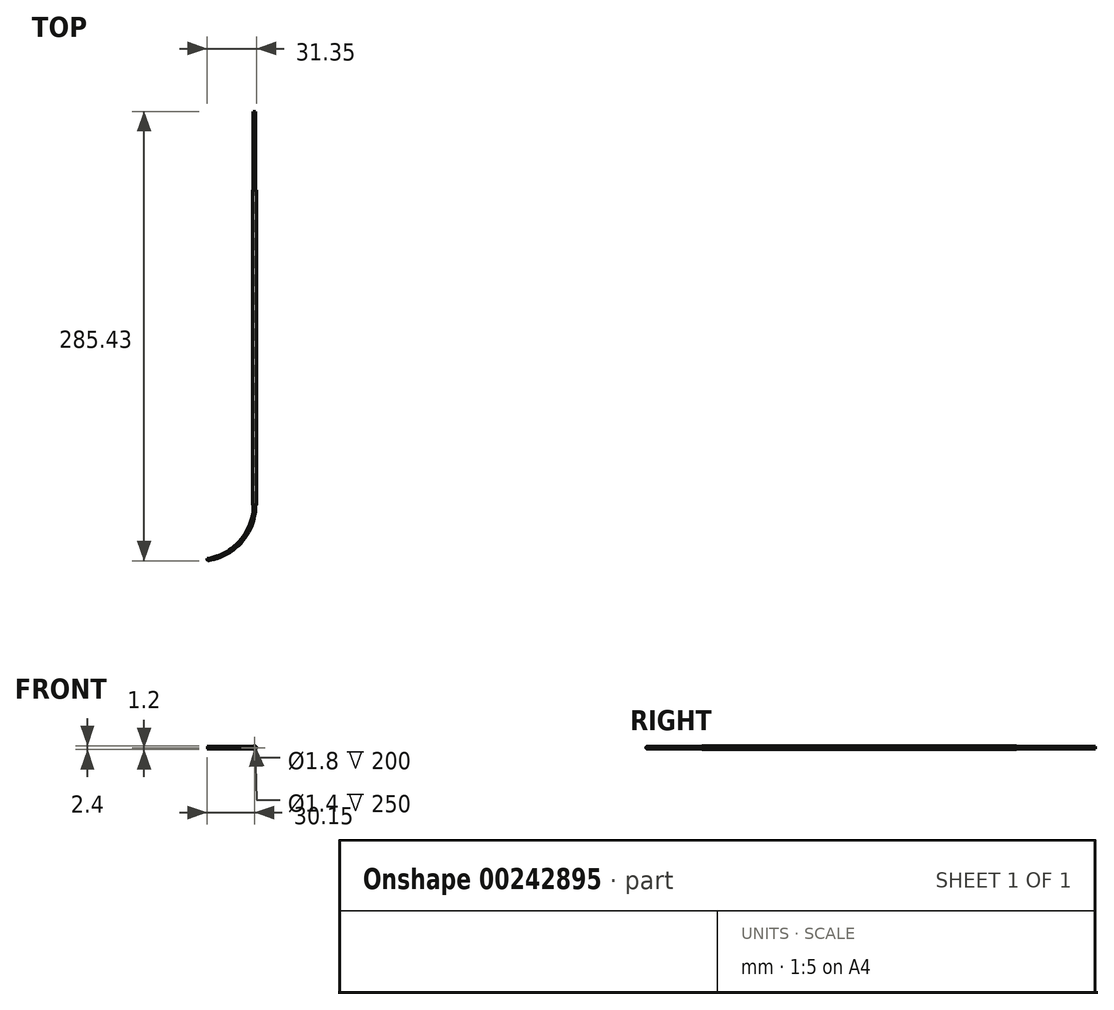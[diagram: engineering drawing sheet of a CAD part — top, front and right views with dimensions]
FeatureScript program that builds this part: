
annotation { "Feature Type Name" : "Feature", "Feature Type Description" : "" }
export const myFeature = defineFeature(function(context is Context, id is Id, definition is map)
    precondition{}
    {
        {
            assignVariable(context, id + "F0", {"name" : "TubeTransmissionLength", "anyValue" : 250});
        }
        {
            var Q0;
            Q0=qCreatedBy(makeId("Front.planeOp"),FACE);
            var sketch = newSketch(context, id + "F1", { "sketchPlane" : qUnion([Q0])});
            skCircle(sketch, "E0", {"center": v(0, 0) * mm, "radius": 0.7 * mm});
            skCircle(sketch, "E1", {"center": v(0, 0) * mm, "radius": 0.8 * mm});
            skSolve(sketch);
        }
        {
            var Q0;
            Q0=qCreatedBy(makeId("Top.planeOp"),FACE);
            var sketch = newSketch(context, id + "F2", { "sketchPlane" : qUnion([Q0])});
            skLineSegment(sketch, "E2", {"start": v(0, 0) * mm, "end": v(0, -250) * mm});
            skLineSegment(sketch, "E3", {"start": v(0, -145.32) * mm, "end": v(0, -250) * mm, "construction": true});
            skLineSegment(sketch, "E4", {"start": v(0, -250) * mm, "end": v(-35, -250) * mm, "construction": true});
            skArc(sketch, "E5", {"start": v(0, -250) * mm, "mid": v(-8.56, -272.93) * mm, "end": v(-30.04, -284.65) * mm});
            skSolve(sketch);
        }
        {
            var Q0;
            Q0=makeQuery(id+"F1.imprint","IMPRINT",FACE,{"disambiguationData":[TD([[makeQuery(id+"F1.imprint","IMPRINT",EDGE,{"derivedFrom":sQuery(id+"F1.wireOp",EDGE,"E0")}),-1.0]])]});
            var Q1;
            Q1=sQuery(id+"F2.wireOp",EDGE,"E2");
            var Q2;
            Q2=sQuery(id+"F2.wireOp",EDGE,"E5");
            sweep(context, id + "F3", {"profiles" : qUnion([Q0]), "path" : qUnion([Q1, Q2])});
        }
        {
            var Q0;
            Q0=makeQuery(id+"F3.opSweep","CAP_FACE",FACE,{"disambiguationData":[OSD([sQuery(id+"F1.wireOp",EDGE,"E0"),sQuery(id+"F1.wireOp",EDGE,"E1"),sQuery(id+"F2.wireOp",VERTEX,"E2.start")])],"isStart":true});
            cPlane(context, id + "F4", {"entities" : qUnion([Q0]), "cplaneType" : CPlaneType.OFFSET, "offset" : 50 * mm, "oppositeDirection" : true, "width" : 150 * mm, "height" : 150 * mm});
        }
        {
            var Q0;
            Q0=qCreatedBy(id+"F4.planeOp",FACE);
            var sketch = newSketch(context, id + "F5", { "sketchPlane" : qUnion([Q0])});
            skCircle(sketch, "E6.0", {"center": v(0, 0) * mm, "radius": 0.8 * mm});
            skCircle(sketch, "E6.1", {"center": v(0, 0) * mm, "radius": 0.7 * mm});
            skCircle(sketch, "E7", {"center": v(0, 0) * mm, "radius": 0.9 * mm});
            skCircle(sketch, "E8", {"center": v(0, 0) * mm, "radius": 1.2 * mm});
            skSolve(sketch);
        }
        {
            var Q0;
            Q0=makeQuery(id+"F5.imprint","IMPRINT",FACE,{"disambiguationData":[TD([[makeQuery(id+"F5.imprint","IMPRINT",EDGE,{"derivedFrom":sQuery(id+"F5.wireOp",EDGE,"E7")}),-1.0]])]});
            var Q1;
            Q1=makeQuery(id+"F3.opSweep","SWEPT_FACE",FACE,{"disambiguationData":[OSD([sQuery(id+"F1.wireOp",EDGE,"E1"),sQuery(id+"F2.wireOp",EDGE,"E2")])]});
            extrude(context, id + "F6", {"entities" : qUnion([Q0]), "oppositeDirection" : true, "endBoundEntityFace" : qUnion([Q1]), "depth" : (getVariable(context, 'TubeTransmissionLength') - 50) * mm});
        }
    });
